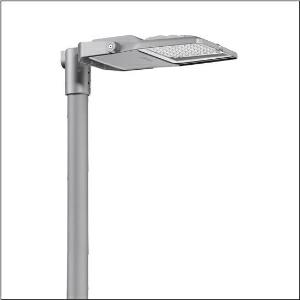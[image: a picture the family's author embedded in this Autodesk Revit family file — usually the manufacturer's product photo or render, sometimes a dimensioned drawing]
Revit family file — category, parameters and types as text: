
# Revit family: floodlight_fl_21_iq_mini___pl52_5xa7772d4d3a_25ab
name_source: partatom
category: Lighting Fixtures
units: mm (PartAtom-declared; Revit-internal decimal feet)

## family parameters
Cut with Voids When Loaded = No
Host = Face
Light Source = No
Part Type = Normal
Room Calculation Point = No
Round Connector Dimension = Use Diameter
Shared = No

## types (1)
- --- (1 x LED, 18610 lm, 143 W, 4000K)
    Apparent Load = 143 VA
    CIE Flux Codes = 26 60 98 100 100
    Color Rendering = 70
    Color Temperature = 4000K
    Default Elevation = 1800 mm
    Description = Floodlight FL 21 iQ mini, floodlight, primary light control with lens, of PMMA, primary optical cover: protective disc, of toughened safety glass, transparent, light distribution: PL52, light emission: direct distribution, installation type: surface-mounted, LED, High Power LED, rated luminous flux: 18.610lm, luminous efficacy: 130lm/W, light colour: 740, colour temperature: 4000K, control: Auto-Match, Temp-Guard, Night-Set, Smart-Wire, Desk-Remote (wireless, voltage-free reading and setting of iQ features in the workshop via application-optimized NFC function/RFID function), optimised constant luminous flux control (CLO 2.0), Light-Fading, Lumen-Switch, with terminal, 6-pole, mains connection: 220..240V, AC, 50/60Hz, start of lifetime: 143W, end of service life: 152W, reduction: 61W, luminaire housing, of diecast aluminium, powder-coated, Siteco® metallic grey (DB 702S), corrosivity category C5 mid according to DIN EN ISO 12944, sealing non-destructively replaceable, please order mast flange separately, mast bracket, of steel, galvanised, powder-coated, protection rating (complete): IP66, insulation class (complete): insulation class II (safety insulation), certification: CE, ENEC, VDE, protection symbol: D, impact resistance: IK08, permissible operating ambient temperature: -40..+40°C, permissible operating ambient temperature for outdoor applications: -40..+50°C, standard: DIN EN 12944, LABS conformity tested according to VDMA 24364:2018-05, packaging unit: 1 piece

Light Distribution: PL52
    Height = 70 mm
    Lamp = 1 x LED
    Lamp Light Flux = 18610 lm
    Lamp Power = 143 W
    Lamp count = 1
    Length = 485 mm
    Luminous efficacy = 130 lm/W
    Manufacturer = Siteco
    ModVariant = No
    Model = 5XA7772D4D3A
    Number of Poles = 1
    OnlyDefault = Yes
    Power Factor = 1
    Product Name = Floodlight FL 21 iQ mini | PL52
    Product group = floodlight | pylon annexe
    ProductGroupID = 6200
    Protection Class = Protection class II
    Protection Degree = IP 66
    RLX_Detail_Level = 1
    RLX_Emergency_Light_Flux = 0 lm
    RLX_Emergency_Type = 0
    RLX_Emergency_Type_DB = No
    RlxData = <blob elided: 101737 chars, md5=2ed1d19a>
    Socket = socket
    Standby Power = 0 W
    System Light Flux = 18610 lm
    System Power = 143 W
    Type Comments = factory setting: luminous flux: 100 % | dim-lin: 254 | 730 mA
    Type Image = l_1007125.jpg
    URL = http://relux.com
    VarID = @adj_113711
    Voltage = 0 V
    Weight = 0.00 kg
    Width = 337 mm

## geometry (parser evidence)
native form markers: Blend x4, Sweep x10
no freeform markers — native parametric forms only
